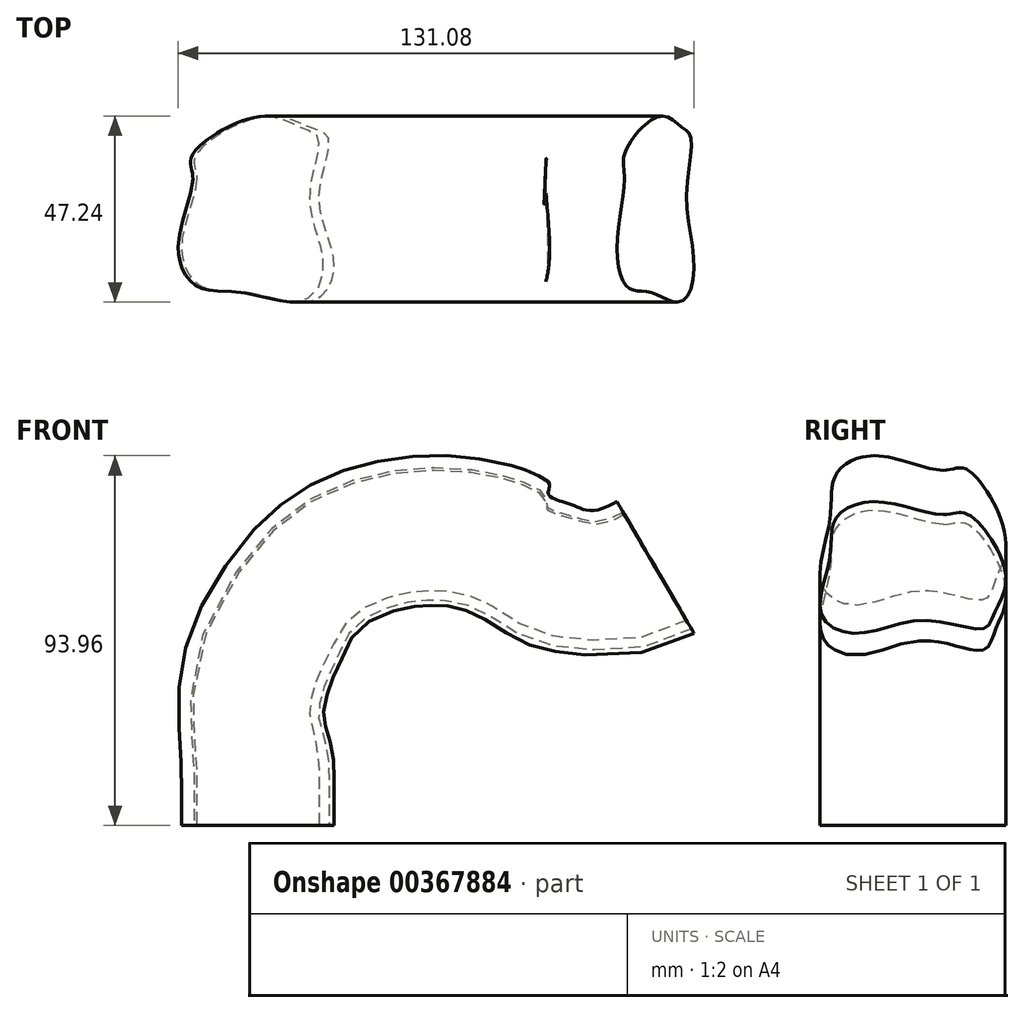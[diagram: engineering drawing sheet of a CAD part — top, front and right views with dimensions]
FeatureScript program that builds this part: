
annotation { "Feature Type Name" : "Feature", "Feature Type Description" : "" }
export const myFeature = defineFeature(function(context is Context, id is Id, definition is map)
    precondition{}
    {
        {
            var Q0;
            Q0=qCreatedBy(makeId("Top.planeOp"),FACE);
            var sketch = newSketch(context, id + "F0", { "sketchPlane" : qUnion([Q0])});
            skFitSpline(sketch, "E0", {"points": [v(-12.63, 11.75) * mm, v(-16.45, -5.29) * mm, v(-11.45, -15.57) * mm, v(0, -17.03) * mm, v(17.03, -19.1) * mm, v(22.32, -9.99) * mm, v(18.5, 7.05) * mm, v(20.85, 22.03) * mm, v(15.86, 24.96) * mm, v(4.7, 27.6) * mm, v(-12.92, 17.62) * mm, v(-12.63, 11.75) * mm]});
            skSolve(sketch);
        }
        {
            var Q0;
            Q0=qCreatedBy(makeId("Front.planeOp"),FACE);
            var sketch = newSketch(context, id + "F1", { "sketchPlane" : qUnion([Q0])});
            skLineSegment(sketch, "E1", {"start": v(0, 0) * mm, "end": v(0, 11.15) * mm});
            skFitSpline(sketch, "E2", {"points": [v(0, 11.15) * mm, v(0, 24.77) * mm, v(2.48, 43.96) * mm, v(18.27, 66.57) * mm, v(35.6, 75.24) * mm, v(53.25, 76.47) * mm, v(69.66, 72.76) * mm, v(81.43, 67.8) * mm, v(87.31, 66.57) * mm, v(99.7, 67.8) * mm, v(112.08, 73.69) * mm], "startDerivative": vector(-0.19, 139.82) * mm, "endDerivative": vector(125.39, 73.74) * mm});
            skSolve(sketch);
        }
        {
            var Q0;
            Q0=makeQuery(id+"F0.imprint","IMPRINT",FACE,{"disambiguationData":[TD([[makeQuery(id+"F0.imprint","IMPRINT",EDGE,{"derivedFrom":sQuery(id+"F0.wireOp",EDGE,"E0")}),1.0]])]});
            var Q1;
            Q1=sQuery(id+"F1.wireOp",EDGE,"E2");
            sweep(context, id + "F2", {"profiles" : qUnion([Q0]), "path" : qUnion([Q1])});
        }
    });
